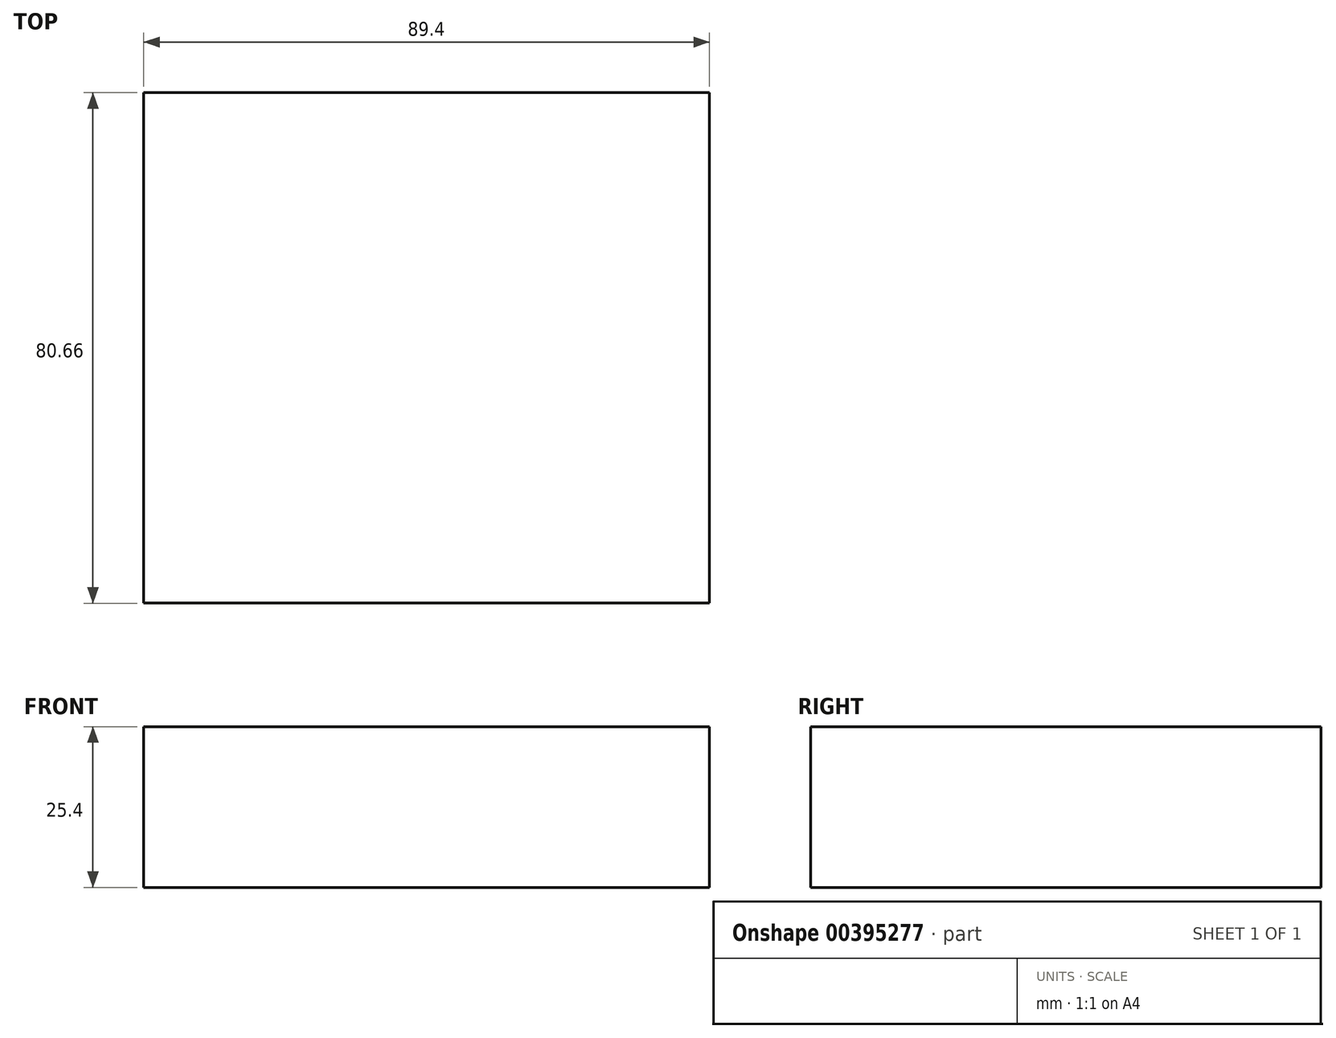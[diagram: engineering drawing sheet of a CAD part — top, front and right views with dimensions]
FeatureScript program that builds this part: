
annotation { "Feature Type Name" : "Feature", "Feature Type Description" : "" }
export const myFeature = defineFeature(function(context is Context, id is Id, definition is map)
    precondition{}
    {
        {
            var Q0;
            Q0=qCreatedBy(makeId("Top.planeOp"),FACE);
            var sketch = newSketch(context, id + "F0", { "sketchPlane" : qUnion([Q0])});
            skLineSegment(sketch, "E0.bottom", {"start": v(-43.7, 39.85) * mm, "end": v(45.69, 39.85) * mm});
            skLineSegment(sketch, "E0.top", {"start": v(-43.7, -40.8) * mm, "end": v(45.69, -40.8) * mm});
            skLineSegment(sketch, "E0.left", {"start": v(-43.7, 39.85) * mm, "end": v(-43.7, -40.8) * mm});
            skLineSegment(sketch, "E0.right", {"start": v(45.69, 39.85) * mm, "end": v(45.69, -40.8) * mm});
            skSolve(sketch);
        }
        {
            var Q0;
            Q0=makeQuery(id+"F0.imprint","IMPRINT",FACE,{"disambiguationData":[TD([[makeQuery(id+"F0.imprint","IMPRINT",EDGE,{"derivedFrom":sQuery(id+"F0.wireOp",EDGE,"E0.bottom")}),-1.0]])]});
            var sketch = newSketch(context, id + "F1", { "sketchPlane" : qUnion([Q0])});
            skSolve(sketch);
        }
        {
            var Q0;
            Q0=makeQuery(id+"F1.imprint","IMPRINT",FACE,{"disambiguationData":[TD([[makeQuery(id+"F1.imprint","IMPRINT",EDGE,{"derivedFrom":makeQuery(id+"F0.imprint","IMPRINT",EDGE,{"derivedFrom":sQuery(id+"F0.wireOp",EDGE,"E0.bottom")})}),-1.0]])]});
            extrude(context, id + "F2", {"entities" : qUnion([Q0]), "depth" : 25.4 * mm});
        }
    });
